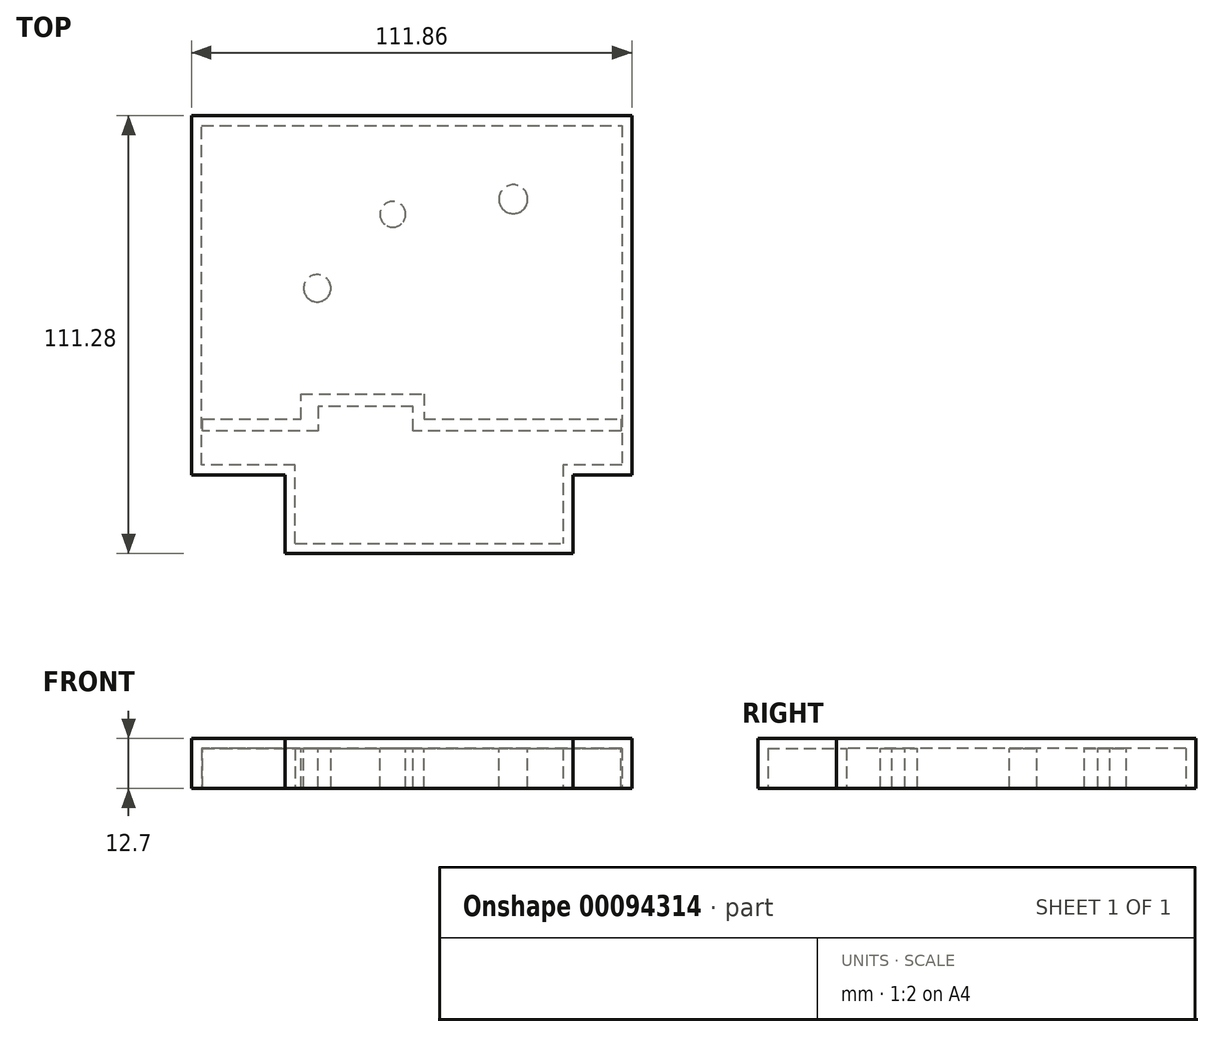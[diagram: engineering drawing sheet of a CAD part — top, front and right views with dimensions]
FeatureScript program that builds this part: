
annotation { "Feature Type Name" : "Feature", "Feature Type Description" : "" }
export const myFeature = defineFeature(function(context is Context, id is Id, definition is map)
    precondition{}
    {
        {
            var Q0;
            Q0=qCreatedBy(makeId("Top.planeOp"),FACE);
            var sketch = newSketch(context, id + "F0", { "sketchPlane" : qUnion([Q0])});
            skLineSegment(sketch, "E0", {"start": v(-59.04, 0) * mm, "end": v(-59.04, 55.74) * mm});
            skLineSegment(sketch, "E1", {"start": v(-59.04, 55.74) * mm, "end": v(52.82, 55.74) * mm});
            skLineSegment(sketch, "E2", {"start": v(52.82, 55.74) * mm, "end": v(52.82, -35.58) * mm});
            skLineSegment(sketch, "E3", {"start": v(52.82, -35.58) * mm, "end": v(37.85, -35.58) * mm});
            skLineSegment(sketch, "E4", {"start": v(37.85, -35.58) * mm, "end": v(37.85, -55.54) * mm});
            skLineSegment(sketch, "E5", {"start": v(-35.26, -55.54) * mm, "end": v(-35.26, -35.58) * mm});
            skLineSegment(sketch, "E6", {"start": v(-35.26, -35.58) * mm, "end": v(-59.04, -35.58) * mm});
            skLineSegment(sketch, "E7", {"start": v(-59.04, -35.58) * mm, "end": v(-59.04, 0) * mm});
            skLineSegment(sketch, "E8", {"start": v(-35.26, -55.54) * mm, "end": v(37.85, -55.54) * mm});
            skSolve(sketch);
        }
        {
            var Q0;
            Q0=makeQuery(id+"F0.imprint","IMPRINT",FACE,{"disambiguationData":[TD([[makeQuery(id+"F0.imprint","IMPRINT",EDGE,{"derivedFrom":sQuery(id+"F0.wireOp",EDGE,"E0")}),-1.0]])]});
            extrude(context, id + "F1", {"entities" : qUnion([Q0]), "depth" : 12.7 * mm});
        }
        {
            var Q0;
            Q0=makeQuery(id+"F1.opExtrude","CAP_FACE",FACE,{"disambiguationData":[OSD([sQuery(id+"F0.wireOp",EDGE,"E0"),sQuery(id+"F0.wireOp",EDGE,"E1"),sQuery(id+"F0.wireOp",EDGE,"E2"),sQuery(id+"F0.wireOp",EDGE,"E3"),sQuery(id+"F0.wireOp",EDGE,"E4"),sQuery(id+"F0.wireOp",EDGE,"E5"),sQuery(id+"F0.wireOp",EDGE,"E6"),sQuery(id+"F0.wireOp",EDGE,"E7"),sQuery(id+"F0.wireOp",EDGE,"E8")])],"isStart":true});
            shell(context, id + "F2", {"entities" : qUnion([Q0]), "thickness" : 2.54 * mm});
        }
        {
            var Q0;
            Q0=makeQuery(id+"F2.opShell","OFFSET_FACE",FACE,{"disambiguationData":[OSD([sQuery(id+"F0.wireOp",EDGE,"E0"),sQuery(id+"F0.wireOp",EDGE,"E1"),sQuery(id+"F0.wireOp",EDGE,"E2"),sQuery(id+"F0.wireOp",EDGE,"E3"),sQuery(id+"F0.wireOp",EDGE,"E4"),sQuery(id+"F0.wireOp",EDGE,"E5"),sQuery(id+"F0.wireOp",EDGE,"E6"),sQuery(id+"F0.wireOp",EDGE,"E7"),sQuery(id+"F0.wireOp",EDGE,"E8")])]});
            var sketch = newSketch(context, id + "F3", { "sketchPlane" : qUnion([Q0])});
            skSolve(sketch);
        }
        {
            var Q0;
            {var subQ2=sQuery(id+"F0.wireOp",EDGE,"E1");Q0=makeQuery(id+"F3.imprint","IMPRINT",FACE,{"disambiguationData":[TD([[makeQuery(id+"F3.imprint","IMPRINT",EDGE,{"derivedFrom":makeQuery(id+"F2.opShell","OFFSET_EDGE",EDGE,{"disambiguationData":[OSD([subQ2]),TDD([makeQuery(id+"F1.opExtrude","CAP_EDGE",EDGE,{"disambiguationData":[OSD([subQ2])],"isStart":false})])]})}),1.0]])]});}
            var sketch = newSketch(context, id + "F4", { "sketchPlane" : qUnion([Q0])});
            skLineSegment(sketch, "E9", {"start": v(-56.23, 21.43) * mm, "end": v(-31.27, 21.43) * mm});
            skLineSegment(sketch, "E10", {"start": v(-31.27, 21.43) * mm, "end": v(-31.27, 14.97) * mm});
            skLineSegment(sketch, "E11", {"start": v(-31.27, 14.97) * mm, "end": v(0, 14.97) * mm});
            skLineSegment(sketch, "E12", {"start": v(0, 14.97) * mm, "end": v(0, 21.43) * mm});
            skLineSegment(sketch, "E13", {"start": v(0, 21.43) * mm, "end": v(50.06, 21.43) * mm});
            skLineSegment(sketch, "E14", {"start": v(50.06, 21.43) * mm, "end": v(50.06, 24.37) * mm});
            skLineSegment(sketch, "E15", {"start": v(50.06, 24.37) * mm, "end": v(-2.79, 24.37) * mm});
            skLineSegment(sketch, "E16", {"start": v(-2.79, 24.37) * mm, "end": v(-2.79, 18.2) * mm});
            skPoint(sketch, "E16.endSnap0", {"position": v(0, 18.2) * mm});
            skLineSegment(sketch, "E17", {"start": v(-2.79, 18.2) * mm, "end": v(-26.87, 18.2) * mm});
            skLineSegment(sketch, "E18", {"start": v(-26.87, 18.2) * mm, "end": v(-26.87, 24.37) * mm});
            skLineSegment(sketch, "E19", {"start": v(-26.87, 24.37) * mm, "end": v(-56.23, 24.37) * mm});
            skLineSegment(sketch, "E20", {"start": v(-56.23, 24.37) * mm, "end": v(-56.23, 21.43) * mm});
            skSolve(sketch);
        }
        {
            var Q0;
            Q0 = qSketchRegion(id + "F4", true);
            var Q1;
            Q1 = qConstructionFilter(qBodyType(qCreatedBy(id + "F4" ,EDGE), BodyType.WIRE), ConstructionObject.NO);
            extrude(context, id + "F5", {"entities" : qUnion([Q0]), "surfaceEntities" : qUnion([Q1]), "depth" : 10.16 * mm});
        }
        {
            var Q0;
            {var subQ2=sQuery(id+"F0.wireOp",EDGE,"E1");Q0=makeQuery(id+"F3.imprint","IMPRINT",FACE,{"disambiguationData":[TD([[makeQuery(id+"F3.imprint","IMPRINT",EDGE,{"derivedFrom":makeQuery(id+"F2.opShell","OFFSET_EDGE",EDGE,{"disambiguationData":[OSD([subQ2]),TDD([makeQuery(id+"F1.opExtrude","CAP_EDGE",EDGE,{"disambiguationData":[OSD([subQ2])],"isStart":false})])]})}),1.0]])]});}
            var sketch = newSketch(context, id + "F6", { "sketchPlane" : qUnion([Q0])});
            skCircle(sketch, "E21", {"center": v(22.7, -34.47) * mm, "radius": 3.66 * mm});
            skCircle(sketch, "E22", {"center": v(-7.93, -30.64) * mm, "radius": 3.26 * mm});
            skCircle(sketch, "E23", {"center": v(-27.1, -11.84) * mm, "radius": 3.46 * mm});
            skSolve(sketch);
        }
        {
            var Q0;
            Q0 = qSketchRegion(id + "F6", true);
            extrude(context, id + "F7", {"entities" : qUnion([Q0]), "operationType" : NewBodyOperationType.ADD, "depth" : 10.16 * mm});
        }
    });
